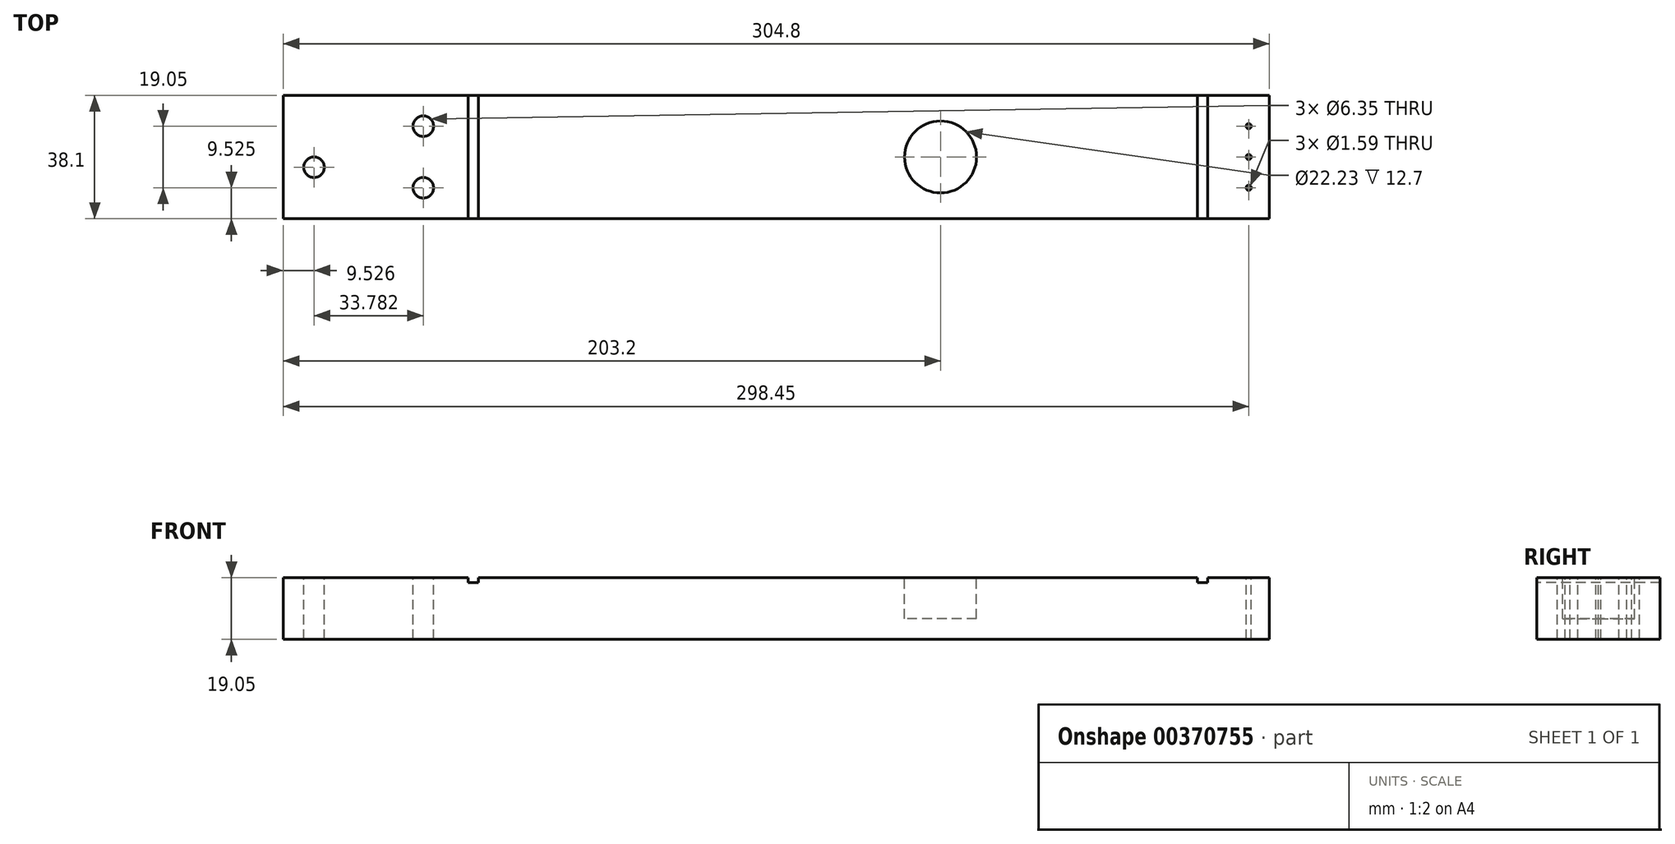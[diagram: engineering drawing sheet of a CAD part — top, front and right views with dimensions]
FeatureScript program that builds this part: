
annotation { "Feature Type Name" : "Feature", "Feature Type Description" : "" }
export const myFeature = defineFeature(function(context is Context, id is Id, definition is map)
    precondition{}
    {
        {
            var Q0;
            Q0=qCreatedBy(makeId("Top.planeOp"),FACE);
            var sketch = newSketch(context, id + "F0", { "sketchPlane" : qUnion([Q0])});
            skLineSegment(sketch, "E0.bottom", {"start": v(-67.92, 19.05) * mm, "end": v(236.88, 19.05) * mm});
            skLineSegment(sketch, "E0.top", {"start": v(-67.92, -19.05) * mm, "end": v(236.88, -19.05) * mm});
            skLineSegment(sketch, "E0.left", {"start": v(-67.92, 19.05) * mm, "end": v(-67.92, -19.05) * mm});
            skLineSegment(sketch, "E0.right", {"start": v(236.88, 19.05) * mm, "end": v(236.88, -19.05) * mm});
            skSolve(sketch);
        }
        {
            var Q0;
            Q0 = qSketchRegion(id + "F0", true);
            extrude(context, id + "F1", {"entities" : qUnion([Q0]), "depth" : 19.05 * mm});
        }
        {
            var Q0;
            Q0=makeQuery(id+"F1.opExtrude","CAP_FACE",FACE,{"disambiguationData":[OSD([sQuery(id+"F0.wireOp",EDGE,"E0.bottom"),sQuery(id+"F0.wireOp",EDGE,"E0.top"),sQuery(id+"F0.wireOp",EDGE,"E0.left"),sQuery(id+"F0.wireOp",EDGE,"E0.right")])],"isStart":false});
            var sketch = newSketch(context, id + "F2", { "sketchPlane" : qUnion([Q0])});
            skCircle(sketch, "E1", {"center": v(135.28, 0) * mm, "radius": 11.11 * mm});
            skSolve(sketch);
        }
        {
            var Q0;
            Q0 = qSketchRegion(id + "F2", true);
            extrude(context, id + "F3", {"entities" : qUnion([Q0]), "operationType" : NewBodyOperationType.REMOVE, "oppositeDirection" : true, "depth" : 12.7 * mm});
        }
        {
            var Q0;
            Q0=makeQuery(id+"F1.opExtrude","CAP_FACE",FACE,{"disambiguationData":[OSD([sQuery(id+"F0.wireOp",EDGE,"E0.bottom"),sQuery(id+"F0.wireOp",EDGE,"E0.top"),sQuery(id+"F0.wireOp",EDGE,"E0.left"),sQuery(id+"F0.wireOp",EDGE,"E0.right")])],"isStart":false});
            var sketch = newSketch(context, id + "F4", { "sketchPlane" : qUnion([Q0])});
            skCircle(sketch, "E2", {"center": v(-58.4, -3.18) * mm, "radius": 3.18 * mm});
            skPoint(sketch, "E3", {"position": v(-58.4, 0) * mm});
            skLineSegment(sketch, "E4", {"start": v(-58.4, 0) * mm, "end": v(135.28, 0) * mm, "construction": true});
            skSolve(sketch);
        }
        {
            var Q0;
            Q0 = qSketchRegion(id + "F4", true);
            extrude(context, id + "F5", {"entities" : qUnion([Q0]), "operationType" : NewBodyOperationType.REMOVE, "endBound" : BoundingType.THROUGH_ALL, "oppositeDirection" : true, "depth" : 25.4 * mm});
        }
        {
            var Q0;
            Q0=makeQuery(id+"F1.opExtrude","CAP_FACE",FACE,{"disambiguationData":[OSD([sQuery(id+"F0.wireOp",EDGE,"E0.bottom"),sQuery(id+"F0.wireOp",EDGE,"E0.top"),sQuery(id+"F0.wireOp",EDGE,"E0.left"),sQuery(id+"F0.wireOp",EDGE,"E0.right")])],"isStart":false});
            var sketch = newSketch(context, id + "F6", { "sketchPlane" : qUnion([Q0])});
            skCircle(sketch, "E5", {"center": v(-24.61, -9.52) * mm, "radius": 3.18 * mm});
            skCircle(sketch, "E6", {"center": v(-24.61, 9.52) * mm, "radius": 3.18 * mm});
            skLineSegment(sketch, "E7", {"start": v(-61.89, 0) * mm, "end": v(-52.24, 0) * mm, "construction": true});
            skLineSegment(sketch, "E8", {"start": v(-28.72, 9.53) * mm, "end": v(-21.71, 9.53) * mm, "construction": true});
            skLineSegment(sketch, "E9", {"start": v(-29.2, -9.53) * mm, "end": v(-21.18, -9.53) * mm, "construction": true});
            skSolve(sketch);
        }
        {
            var Q0;
            Q0 = qSketchRegion(id + "F6", true);
            extrude(context, id + "F7", {"entities" : qUnion([Q0]), "operationType" : NewBodyOperationType.REMOVE, "endBound" : BoundingType.THROUGH_ALL, "oppositeDirection" : true, "depth" : 25.4 * mm});
        }
        {
            var Q0;
            Q0=makeQuery(id+"F1.opExtrude","CAP_FACE",FACE,{"disambiguationData":[OSD([sQuery(id+"F0.wireOp",EDGE,"E0.bottom"),sQuery(id+"F0.wireOp",EDGE,"E0.top"),sQuery(id+"F0.wireOp",EDGE,"E0.left"),sQuery(id+"F0.wireOp",EDGE,"E0.right")])],"isStart":false});
            var sketch = newSketch(context, id + "F8", { "sketchPlane" : qUnion([Q0])});
            skLineSegment(sketch, "E10", {"start": v(230.53, 9.52) * mm, "end": v(230.53, -9.52) * mm, "construction": true});
            skCircle(sketch, "E11", {"center": v(230.53, 9.52) * mm, "radius": 0.8 * mm});
            skCircle(sketch, "E12", {"center": v(230.53, 0) * mm, "radius": 0.8 * mm});
            skCircle(sketch, "E13", {"center": v(230.53, -9.52) * mm, "radius": 0.8 * mm});
            skLineSegment(sketch, "E14", {"start": v(230.53, 0) * mm, "end": v(135.28, 0) * mm, "construction": true});
            skSolve(sketch);
        }
        {
            var Q0;
            Q0 = qSketchRegion(id + "F8", true);
            extrude(context, id + "F9", {"entities" : qUnion([Q0]), "operationType" : NewBodyOperationType.REMOVE, "endBound" : BoundingType.THROUGH_ALL, "oppositeDirection" : true, "depth" : 25.4 * mm});
        }
        {
            var Q0;
            Q0=makeQuery(id+"F1.opExtrude","SWEPT_FACE",FACE,{"disambiguationData":[OSD([sQuery(id+"F0.wireOp",EDGE,"E0.top")])]});
            var sketch = newSketch(context, id + "F10", { "sketchPlane" : qUnion([Q0])});
            skLineSegment(sketch, "E15.bottom", {"start": v(-10.77, 19.05) * mm, "end": v(-7.6, 19.05) * mm});
            skLineSegment(sketch, "E15.top", {"start": v(-10.77, 17.46) * mm, "end": v(-7.6, 17.46) * mm});
            skLineSegment(sketch, "E15.left", {"start": v(-10.77, 19.05) * mm, "end": v(-10.77, 17.46) * mm});
            skLineSegment(sketch, "E15.right", {"start": v(-7.6, 19.05) * mm, "end": v(-7.6, 17.46) * mm});
            skLineSegment(sketch, "E16.bottom", {"start": v(214.66, 19.05) * mm, "end": v(217.83, 19.05) * mm});
            skLineSegment(sketch, "E16.top", {"start": v(214.66, 17.46) * mm, "end": v(217.83, 17.46) * mm});
            skLineSegment(sketch, "E16.left", {"start": v(214.66, 19.05) * mm, "end": v(214.66, 17.46) * mm});
            skLineSegment(sketch, "E16.right", {"start": v(217.83, 19.05) * mm, "end": v(217.83, 17.46) * mm});
            skSolve(sketch);
        }
        {
            var Q0;
            Q0 = qSketchRegion(id + "F10", true);
            extrude(context, id + "F11", {"entities" : qUnion([Q0]), "operationType" : NewBodyOperationType.REMOVE, "endBound" : BoundingType.THROUGH_ALL, "oppositeDirection" : true, "depth" : 25.4 * mm});
        }
    });
